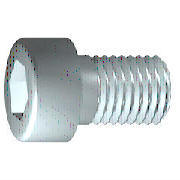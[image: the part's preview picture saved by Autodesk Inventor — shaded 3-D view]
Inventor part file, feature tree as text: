
AUTODESK INVENTOR PART (.ipt)
format: ipt  version: 2024.3 (Build 283343000, 343)  size: 193,024 bytes
history: native  units: mm (DEFAULTED — no unit token found)
features: extrude x1, plane x1, fillet x1
ambient origin geometry x7: Origin, YZ Plane, XY Plane, X Axis, Y Axis, Z Axis, Center Point
bodies: Solid1 (feature_tree), Body (feature_tree)
feature tree (3):
  extrude  "Slot"  Depth=14.0mm
  plane  "Work Plane1"
  fillet  "Fillet2"  Radius=0.49086mm
